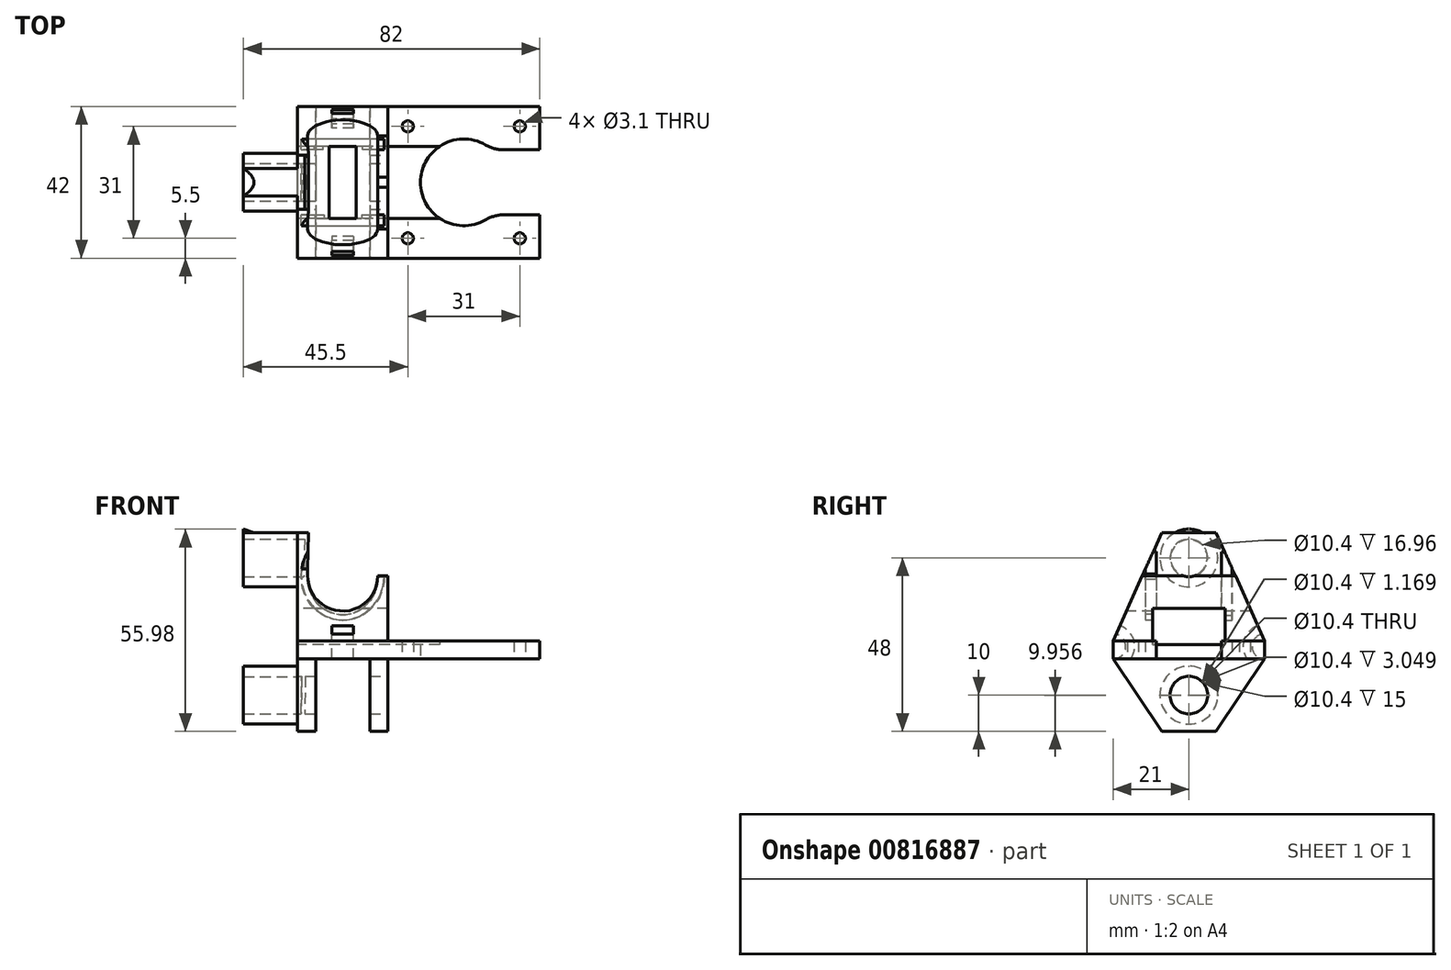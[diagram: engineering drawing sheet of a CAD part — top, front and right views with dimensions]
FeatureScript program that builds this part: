
annotation { "Feature Type Name" : "Feature", "Feature Type Description" : "" }
export const myFeature = defineFeature(function(context is Context, id is Id, definition is map)
    precondition{}
    {
        {
            var Q0;
            Q0=qCreatedBy(makeId("Top.planeOp"),FACE);
            var sketch = newSketch(context, id + "F0", { "sketchPlane" : qUnion([Q0])});
            skLineSegment(sketch, "E0.bottom", {"start": v(0, 0) * mm, "end": v(42, 0) * mm});
            skLineSegment(sketch, "E0.top", {"start": v(0, 42) * mm, "end": v(42, 42) * mm});
            skLineSegment(sketch, "E0.left", {"start": v(0, 0) * mm, "end": v(0, 42) * mm});
            skLineSegment(sketch, "E0.right", {"start": v(42, 0) * mm, "end": v(42, 12) * mm});
            skArc(sketch, "E1", {"start": v(27.05, 31.36) * mm, "mid": v(9, 21) * mm, "end": v(27.05, 10.64) * mm});
            skPoint(sketch, "E1.centerSnap0", {"position": v(21, 42) * mm});
            skPoint(sketch, "E1.centerSnap1", {"position": v(42, 21) * mm});
            skCircle(sketch, "E2", {"center": v(5.5, 36.5) * mm, "radius": 1.55 * mm});
            skCircle(sketch, "E3", {"center": v(36.5, 36.5) * mm, "radius": 1.55 * mm});
            skCircle(sketch, "E4", {"center": v(36.5, 5.5) * mm, "radius": 1.55 * mm});
            skCircle(sketch, "E5", {"center": v(5.5, 5.5) * mm, "radius": 1.55 * mm});
            skLineSegment(sketch, "E6", {"start": v(42, 30) * mm, "end": v(32.1, 30) * mm});
            skLineSegment(sketch, "E7", {"start": v(42, 12) * mm, "end": v(32.1, 12) * mm});
            skLineSegment(sketch, "E8.trimOffspring", {"start": v(42, 30) * mm, "end": v(42, 42) * mm});
            skPoint(sketch, "E9.visualSharp", {"position": v(28.94, 30) * mm});
            skArc(sketch, "E9.filletArc", {"start": v(27.05, 31.36) * mm, "mid": v(29.48, 30.35) * mm, "end": v(32.1, 30) * mm});
            skPoint(sketch, "E10.visualSharp", {"position": v(28.94, 12) * mm});
            skArc(sketch, "E10.filletArc", {"start": v(32.1, 12) * mm, "mid": v(29.48, 11.65) * mm, "end": v(27.05, 10.64) * mm});
            skSolve(sketch);
        }
        {
            var Q0;
            Q0 = qSketchRegion(id + "F0", true);
            extrude(context, id + "F1", {"entities" : qUnion([Q0]), "depth" : 5 * mm, "offsetDistance" : 25 * mm});
        }
        {
            var Q0;
            Q0=makeQuery(id+"F1.opExtrude","SWEPT_FACE",FACE,{"disambiguationData":[OSD([sQuery(id+"F0.wireOp",EDGE,"E0.left")])]});
            var sketch = newSketch(context, id + "F2", { "sketchPlane" : qUnion([Q0])});
            skLineSegment(sketch, "E11", {"start": v(-42, 5) * mm, "end": v(-28.5, 35) * mm});
            skLineSegment(sketch, "E12", {"start": v(-28.5, 35) * mm, "end": v(-13.5, 35) * mm});
            skLineSegment(sketch, "E13", {"start": v(-13.5, 35) * mm, "end": v(0, 5) * mm});
            skLineSegment(sketch, "E14", {"start": v(0, 5) * mm, "end": v(0, 0) * mm});
            skLineSegment(sketch, "E15", {"start": v(0, 0) * mm, "end": v(-13.5, -20) * mm});
            skLineSegment(sketch, "E16", {"start": v(-13.5, -20) * mm, "end": v(-28.5, -20) * mm});
            skLineSegment(sketch, "E17", {"start": v(-28.5, -20) * mm, "end": v(-42, 0) * mm});
            skLineSegment(sketch, "E18", {"start": v(-42, 0) * mm, "end": v(-42, 5) * mm});
            skLineSegment(sketch, "E19.bottom", {"start": v(-31, 5) * mm, "end": v(-11, 5) * mm});
            skLineSegment(sketch, "E19.top", {"start": v(-31, 13) * mm, "end": v(-11, 13) * mm});
            skLineSegment(sketch, "E19.left", {"start": v(-31, 5) * mm, "end": v(-31, 13) * mm});
            skLineSegment(sketch, "E19.right", {"start": v(-11, 5) * mm, "end": v(-11, 13) * mm});
            skCircle(sketch, "E20", {"center": v(-21, 28) * mm, "radius": 5.2 * mm});
            skPoint(sketch, "E20.centerSnap0", {"position": v(-21, 13) * mm});
            skCircle(sketch, "E21", {"center": v(-21, -10) * mm, "radius": 5.2 * mm});
            skPoint(sketch, "E21.centerSnap0", {"position": v(-21, 0) * mm});
            skSolve(sketch);
        }
        {
            var Q0;
            Q0 = qSketchRegion(id + "F2", true);
            extrude(context, id + "F3", {"entities" : qUnion([Q0]), "operationType" : NewBodyOperationType.ADD, "depth" : 25 * mm, "offsetDistance" : 25 * mm});
        }
        {
            var Q0;
            Q0=makeQuery(id+"F3.boolean.opBoolean","MERGE",FACE,{"derivedFrom":[makeQuery(id+"F1.opExtrude","SWEPT_FACE",FACE,{"disambiguationData":[OSD([sQuery(id+"F0.wireOp",EDGE,"E0.bottom")])]}),makeQuery(id+"F3.opExtrude","SWEPT_FACE",FACE,{"disambiguationData":[OSD([sQuery(id+"F2.wireOp",EDGE,"E14")])]})]});
            var sketch = newSketch(context, id + "F4", { "sketchPlane" : qUnion([Q0])});
            skArc(sketch, "E22", {"start": v(-22.25, 23.2) * mm, "mid": v(-12.6, 13.25) * mm, "end": v(-2.75, 23) * mm});
            skLineSegment(sketch, "E23.bottom", {"start": v(-20, 0) * mm, "end": v(-5, 0) * mm});
            skLineSegment(sketch, "E23.top", {"start": v(-20, -20) * mm, "end": v(-5, -20) * mm});
            skLineSegment(sketch, "E23.left", {"start": v(-20, 0) * mm, "end": v(-20, -20) * mm});
            skLineSegment(sketch, "E23.right", {"start": v(-5, 0) * mm, "end": v(-5, -20) * mm});
            skLineSegment(sketch, "E24", {"start": v(-2.75, 23) * mm, "end": v(0, 23) * mm});
            skLineSegment(sketch, "E25", {"start": v(0, 23) * mm, "end": v(0, 35.11) * mm});
            skLineSegment(sketch, "E26", {"start": v(0, 35.11) * mm, "end": v(-22, 35.11) * mm});
            skLineSegment(sketch, "E27", {"start": v(-22, 35.11) * mm, "end": v(-22.25, 23) * mm});
            skSolve(sketch);
        }
        {
            var Q0;
            Q0 = qSketchRegion(id + "F4", true);
            extrude(context, id + "F5", {"entities" : qUnion([Q0]), "operationType" : NewBodyOperationType.REMOVE, "oppositeDirection" : true, "depth" : 69 * mm, "offsetDistance" : 25 * mm});
        }
        {
            var Q0;
            Q0=makeQuery(id+"F3.opExtrude","CAP_FACE",FACE,{"disambiguationData":[OSD([sQuery(id+"F2.wireOp",EDGE,"E11"),sQuery(id+"F2.wireOp",EDGE,"E12"),sQuery(id+"F2.wireOp",EDGE,"E13"),sQuery(id+"F2.wireOp",EDGE,"E14"),sQuery(id+"F2.wireOp",EDGE,"E15"),sQuery(id+"F2.wireOp",EDGE,"E16"),sQuery(id+"F2.wireOp",EDGE,"E17"),sQuery(id+"F2.wireOp",EDGE,"E18"),sQuery(id+"F2.wireOp",EDGE,"E19.bottom"),sQuery(id+"F2.wireOp",EDGE,"E19.top"),sQuery(id+"F2.wireOp",EDGE,"E19.left"),sQuery(id+"F2.wireOp",EDGE,"E19.right"),sQuery(id+"F2.wireOp",EDGE,"E20"),sQuery(id+"F2.wireOp",EDGE,"E21")])],"isStart":false});
            var sketch = newSketch(context, id + "F6", { "sketchPlane" : qUnion([Q0])});
            skArc(sketch, "E28", {"start": v(-26.2, 28) * mm, "mid": v(-21, 22.8) * mm, "end": v(-15.8, 28) * mm});
            skArc(sketch, "E29", {"start": v(-29, 28) * mm, "mid": v(-21, 19.98) * mm, "end": v(-13, 28) * mm});
            skArc(sketch, "E30", {"start": v(-29, -10) * mm, "mid": v(-21, -18) * mm, "end": v(-13, -10) * mm});
            skArc(sketch, "E31", {"start": v(-26.2, -10) * mm, "mid": v(-21, -15.24) * mm, "end": v(-15.8, -10) * mm});
            skArc(sketch, "E32", {"start": v(-13, 28) * mm, "mid": v(-21, 35.98) * mm, "end": v(-29, 28) * mm});
            skArc(sketch, "E33", {"start": v(-15.8, 28) * mm, "mid": v(-21, 33.2) * mm, "end": v(-26.2, 28) * mm});
            skArc(sketch, "E34", {"start": v(-13, -10) * mm, "mid": v(-21, -2) * mm, "end": v(-29, -10) * mm});
            skArc(sketch, "E35", {"start": v(-15.8, -10) * mm, "mid": v(-21, -4.84) * mm, "end": v(-26.2, -10) * mm});
            skSolve(sketch);
        }
        {
            var Q0;
            Q0 = qSketchRegion(id + "F6", true);
            extrude(context, id + "F7", {"entities" : qUnion([Q0]), "operationType" : NewBodyOperationType.ADD, "depth" : 15 * mm, "offsetDistance" : 25 * mm});
        }
        {
            var Q0;
            Q0=makeQuery(id+"F3.boolean.opBoolean","MERGE",FACE,{"derivedFrom":[makeQuery(id+"F1.opExtrude","SWEPT_FACE",FACE,{"disambiguationData":[OSD([sQuery(id+"F0.wireOp",EDGE,"E0.bottom")])]}),makeQuery(id+"F3.opExtrude","SWEPT_FACE",FACE,{"disambiguationData":[OSD([sQuery(id+"F2.wireOp",EDGE,"E14")])]})]});
            cPlane(context, id + "F8", {"entities" : qUnion([Q0]), "cplaneType" : CPlaneType.OFFSET, "offset" : 9 * mm, "oppositeDirection" : true, "width" : 150 * mm, "height" : 150 * mm});
        }
        {
            var Q0;
            Q0=qCreatedBy(id+"F8.planeOp",FACE);
            var sketch = newSketch(context, id + "F9", { "sketchPlane" : qUnion([Q0])});
            skEllipse(sketch, "E36", {"center": v(-12.5, 23.1) * mm, "majorRadius": 10.75 * mm, "minorRadius": 9.75 * mm, "majorAxis": v(0, -1)});
            skEllipse(sketch, "E37", {"center": v(-12.5, 23.1) * mm, "majorRadius": 12.25 * mm, "minorRadius": 11.5 * mm, "majorAxis": v(0, -1)});
            skSolve(sketch);
        }
        {
            var Q0;
            Q0 = qSketchRegion(id + "F9", true);
            extrude(context, id + "F10", {"entities" : qUnion([Q0]), "operationType" : NewBodyOperationType.REMOVE, "oppositeDirection" : true, "depth" : 3 * mm, "offsetDistance" : 25 * mm});
        }
        {
            var Q0;
            Q0=makeQuery(id+"F3.boolean.opBoolean","MERGE",FACE,{"derivedFrom":[makeQuery(id+"F1.opExtrude","SWEPT_FACE",FACE,{"disambiguationData":[OSD([sQuery(id+"F0.wireOp",EDGE,"E0.top")])]}),makeQuery(id+"F3.opExtrude","SWEPT_FACE",FACE,{"disambiguationData":[OSD([sQuery(id+"F2.wireOp",EDGE,"E18")])]})]});
            cPlane(context, id + "F11", {"entities" : qUnion([Q0]), "cplaneType" : CPlaneType.OFFSET, "offset" : 9 * mm, "oppositeDirection" : true, "width" : 150 * mm, "height" : 150 * mm});
        }
        {
            var Q0;
            Q0=qCreatedBy(id+"F11.planeOp",FACE);
            var sketch = newSketch(context, id + "F12", { "sketchPlane" : qUnion([Q0])});
            skEllipse(sketch, "E38", {"center": v(12.5, 22.9) * mm, "majorRadius": 10.75 * mm, "minorRadius": 9.75 * mm, "majorAxis": v(0, -1)});
            skEllipse(sketch, "E39", {"center": v(12.5, 22.9) * mm, "majorRadius": 12.25 * mm, "minorRadius": 11.5 * mm, "majorAxis": v(0, -1)});
            skSolve(sketch);
        }
        {
            var Q0;
            Q0 = qSketchRegion(id + "F12", true);
            extrude(context, id + "F13", {"entities" : qUnion([Q0]), "operationType" : NewBodyOperationType.REMOVE, "oppositeDirection" : true, "depth" : 3 * mm, "offsetDistance" : 25 * mm});
        }
        {
            var Q0;
            {var subQ0=sQuery(id+"F0.wireOp",EDGE,"E0.bottom");var subQ1=sQuery(id+"F2.wireOp",EDGE,"E21");var subQ2=sQuery(id+"F2.wireOp",EDGE,"E20");var subQ3=sQuery(id+"F2.wireOp",EDGE,"E19.top");var subQ4=sQuery(id+"F2.wireOp",EDGE,"E18");var subQ5=sQuery(id+"F2.wireOp",EDGE,"E17");var subQ6=sQuery(id+"F2.wireOp",EDGE,"E11");var subQ7=sQuery(id+"F6.wireOp",EDGE,"j4Je13ar-cUgQ-P9dA-qSxm-OQoqqm40TVXU");var subQ8=sQuery(id+"F2.wireOp",EDGE,"E19.right");var subQ9=sQuery(id+"F0.wireOp",EDGE,"E0.top");var subQ10=sQuery(id+"F6.wireOp",EDGE,"E31");var subQ11=sQuery(id+"F6.wireOp",EDGE,"E30");var subQ12=sQuery(id+"F6.wireOp",EDGE,"HeXZzPOW-6o9y-4eNm-dmXj-kad8RJGDjiKm");var subQ13=sQuery(id+"F2.wireOp",EDGE,"E19.left");var subQ14=sQuery(id+"F2.wireOp",EDGE,"E19.bottom");var subQ15=sQuery(id+"F2.wireOp",EDGE,"E15");var subQ16=sQuery(id+"F2.wireOp",EDGE,"E16");var subQ17=sQuery(id+"F2.wireOp",EDGE,"E14");var subQ18=sQuery(id+"F2.wireOp",EDGE,"E13");var subQ19=sQuery(id+"F2.wireOp",EDGE,"E12");var subQ20=makeQuery(id+"F3.opExtrude","CAP_FACE",FACE,{"disambiguationData":[OSD([subQ6,subQ19,subQ18,subQ17,subQ15,subQ16,subQ5,subQ4,subQ14,subQ3,subQ13,subQ8,subQ2,subQ1])],"isStart":false});Q0=makeQuery(id+"F7.boolean.opBoolean","SPLIT",FACE,{"disambiguationData":[TD([makeQuery(id+"F1.opExtrude","SWEPT_FACE",FACE,{"disambiguationData":[OSD([subQ0])]}),makeQuery(id+"F1.opExtrude","CAP_FACE",FACE,{"disambiguationData":[OSD([subQ0,subQ9,sQuery(id+"F0.wireOp",EDGE,"E0.left"),sQuery(id+"F0.wireOp",EDGE,"E0.right"),sQuery(id+"F0.wireOp",EDGE,"E1"),sQuery(id+"F0.wireOp",EDGE,"E2"),sQuery(id+"F0.wireOp",EDGE,"E3"),sQuery(id+"F0.wireOp",EDGE,"E4"),sQuery(id+"F0.wireOp",EDGE,"E5"),sQuery(id+"F0.wireOp",EDGE,"E6"),sQuery(id+"F0.wireOp",EDGE,"E7"),sQuery(id+"F0.wireOp",EDGE,"E8.trimOffspring"),sQuery(id+"F0.wireOp",EDGE,"E9.filletArc"),sQuery(id+"F0.wireOp",EDGE,"E10.filletArc")])],"isStart":false}),makeQuery(id+"F1.opExtrude","SWEPT_FACE",FACE,{"disambiguationData":[OSD([subQ9])]}),makeQuery(id+"F3.opExtrude","SWEPT_FACE",FACE,{"disambiguationData":[OSD([subQ6])]}),subQ20,makeQuery(id+"F3.opExtrude","SWEPT_FACE",FACE,{"disambiguationData":[OSD([subQ19])]}),makeQuery(id+"F3.opExtrude","SWEPT_FACE",FACE,{"disambiguationData":[OSD([subQ18])]}),makeQuery(id+"F3.opExtrude","SWEPT_FACE",FACE,{"disambiguationData":[OSD([subQ17])]}),makeQuery(id+"F3.opExtrude","SWEPT_FACE",FACE,{"disambiguationData":[OSD([subQ15])]}),makeQuery(id+"F3.opExtrude","SWEPT_FACE",FACE,{"disambiguationData":[OSD([subQ16])]}),makeQuery(id+"F3.opExtrude","SWEPT_FACE",FACE,{"disambiguationData":[OSD([subQ5])]}),makeQuery(id+"F3.opExtrude","SWEPT_FACE",FACE,{"disambiguationData":[OSD([subQ4])]}),makeQuery(id+"F3.opExtrude","SWEPT_FACE",FACE,{"disambiguationData":[OSD([subQ14])]}),makeQuery(id+"F3.opExtrude","SWEPT_FACE",FACE,{"disambiguationData":[OSD([subQ3])]}),makeQuery(id+"F3.opExtrude","SWEPT_FACE",FACE,{"disambiguationData":[OSD([subQ13])]}),makeQuery(id+"F3.opExtrude","SWEPT_FACE",FACE,{"disambiguationData":[OSD([subQ8])]}),makeQuery(id+"F3.opExtrude","SWEPT_FACE",FACE,{"disambiguationData":[OSD([subQ2])]}),makeQuery(id+"F3.opExtrude","SWEPT_FACE",FACE,{"disambiguationData":[OSD([subQ1])]}),makeQuery(id+"F7.opExtrude","SWEPT_FACE",FACE,{"disambiguationData":[OSD([sQuery(id+"F6.wireOp",EDGE,"1yMtYrWf-nUJP-NBpX-7LZj-JU54sDcnYQW7")])]}),makeQuery(id+"F7.opExtrude","SWEPT_FACE",FACE,{"disambiguationData":[OSD([sQuery(id+"F6.wireOp",EDGE,"Y7kda9e2-xFBF-SAdd-E8dt-nTogyCoIO5LO")])]}),makeQuery(id+"F7.opExtrude","SWEPT_FACE",FACE,{"disambiguationData":[OSD([sQuery(id+"F6.wireOp",EDGE,"E28")])]}),makeQuery(id+"F7.opExtrude","SWEPT_FACE",FACE,{"disambiguationData":[OSD([sQuery(id+"F6.wireOp",EDGE,"E29")])]}),makeQuery(id+"F7.opExtrude","SWEPT_FACE",FACE,{"disambiguationData":[OSD([subQ12])]}),makeQuery(id+"F7.opExtrude","CAP_FACE",FACE,{"disambiguationData":[OSD([subQ12,subQ11,subQ7,subQ10])],"isStart":true}),makeQuery(id+"F7.opExtrude","SWEPT_FACE",FACE,{"disambiguationData":[OSD([subQ11])]}),makeQuery(id+"F7.opExtrude","SWEPT_FACE",FACE,{"disambiguationData":[OSD([subQ7])]}),makeQuery(id+"F7.opExtrude","SWEPT_FACE",FACE,{"disambiguationData":[OSD([subQ10])]})])],"derivedFrom":subQ20});}
            cPlane(context, id + "F14", {"entities" : qUnion([Q0]), "cplaneType" : CPlaneType.OFFSET, "offset" : 9.5 * mm, "oppositeDirection" : true, "width" : 150 * mm, "height" : 150 * mm});
        }
        {
            var Q0;
            Q0=qCreatedBy(id+"F14.planeOp",FACE);
            var sketch = newSketch(context, id + "F15", { "sketchPlane" : qUnion([Q0])});
            skCircle(sketch, "E40", {"center": v(0, 3.5) * mm, "radius": 3.5 * mm});
            skCircle(sketch, "E41", {"center": v(0, 3.5) * mm, "radius": 6 * mm});
            skCircle(sketch, "E42", {"center": v(-42, 3.5) * mm, "radius": 3.5 * mm});
            skCircle(sketch, "E43", {"center": v(-42, 3.5) * mm, "radius": 6 * mm});
            skSolve(sketch);
        }
        {
            var Q0;
            Q0 = qSketchRegion(id + "F15", true);
            extrude(context, id + "F16", {"entities" : qUnion([Q0]), "operationType" : NewBodyOperationType.REMOVE, "oppositeDirection" : true, "depth" : 6 * mm, "offsetDistance" : 25 * mm});
        }
        {
            var Q0;
            {var subQ0=sQuery(id+"F2.wireOp",EDGE,"E16");var subQ1=sQuery(id+"F2.wireOp",EDGE,"E14");var subQ2=sQuery(id+"F2.wireOp",EDGE,"E13");var subQ3=sQuery(id+"F2.wireOp",EDGE,"E12");var subQ4=sQuery(id+"F2.wireOp",EDGE,"E15");var subQ5=sQuery(id+"F0.wireOp",EDGE,"E0.bottom");var subQ6=sQuery(id+"F2.wireOp",EDGE,"E19.bottom");var subQ7=sQuery(id+"F2.wireOp",EDGE,"E17");var subQ9=sQuery(id+"F2.wireOp",EDGE,"E19.left");var subQ12=sQuery(id+"F2.wireOp",EDGE,"E19.right");var subQ13=sQuery(id+"F2.wireOp",EDGE,"E11");var subQ14=sQuery(id+"F2.wireOp",EDGE,"E18");var subQ15=sQuery(id+"F2.wireOp",EDGE,"E19.top");Q0=makeQuery(id+"F7.boolean.opBoolean","SPLIT",FACE,{"disambiguationData":[TD([makeQuery(id+"F1.opExtrude","SWEPT_FACE",FACE,{"disambiguationData":[OSD([subQ5])]})])],"derivedFrom":makeQuery(id+"F3.opExtrude","CAP_FACE",FACE,{"disambiguationData":[OSD([subQ13,subQ3,subQ2,subQ1,subQ4,subQ0,subQ7,subQ14,subQ6,subQ15,subQ9,subQ12,sQuery(id+"F2.wireOp",EDGE,"E20"),sQuery(id+"F2.wireOp",EDGE,"E21")])],"isStart":false})});}
            var sketch = newSketch(context, id + "F17", { "sketchPlane" : qUnion([Q0])});
            skLineSegment(sketch, "E44.bottom", {"start": v(-31, 4) * mm, "end": v(-11, 4) * mm});
            skLineSegment(sketch, "E44.top", {"start": v(-31, 14) * mm, "end": v(-11, 14) * mm});
            skLineSegment(sketch, "E44.left", {"start": v(-31, 4) * mm, "end": v(-31, 14) * mm});
            skLineSegment(sketch, "E44.right", {"start": v(-11, 4) * mm, "end": v(-11, 14) * mm});
            skSolve(sketch);
        }
        {
            var Q0;
            Q0 = qSketchRegion(id + "F17", true);
            extrude(context, id + "F18", {"entities" : qUnion([Q0]), "operationType" : NewBodyOperationType.REMOVE, "oppositeDirection" : true, "depth" : 50 * mm, "offsetDistance" : 25 * mm});
        }
        {
            var Q0;
            {var subQ0=sQuery(id+"F6.wireOp",EDGE,"E32");var subQ1=sQuery(id+"F6.wireOp",EDGE,"E29");Q0=makeQuery(id+"F7.boolean.opBoolean","SPLIT",EDGE,{"disambiguationData":[topologyDisambiguationEdgeConnected([makeQuery(id+"F3.opExtrude","CAP_FACE",FACE,{"disambiguationData":[OSD([sQuery(id+"F2.wireOp",EDGE,"E11"),sQuery(id+"F2.wireOp",EDGE,"E12"),sQuery(id+"F2.wireOp",EDGE,"E13"),sQuery(id+"F2.wireOp",EDGE,"E14"),sQuery(id+"F2.wireOp",EDGE,"E15"),sQuery(id+"F2.wireOp",EDGE,"E16"),sQuery(id+"F2.wireOp",EDGE,"E17"),sQuery(id+"F2.wireOp",EDGE,"E18"),sQuery(id+"F2.wireOp",EDGE,"E19.bottom"),sQuery(id+"F2.wireOp",EDGE,"E19.top"),sQuery(id+"F2.wireOp",EDGE,"E19.left"),sQuery(id+"F2.wireOp",EDGE,"E19.right"),sQuery(id+"F2.wireOp",EDGE,"E20"),sQuery(id+"F2.wireOp",EDGE,"E21")])],"isStart":false})])],"derivedFrom":makeQuery(id+"F7.opExtrude","CAP_EDGE",EDGE,{"disambiguationData":[OSD([subQ1,subQ0])],"isStart":true})});}
            var Q1;
            Q1=makeQuery(id+"F7.opExtrude","CAP_EDGE",EDGE,{"disambiguationData":[OSD([sQuery(id+"F6.wireOp",EDGE,"E30"),sQuery(id+"F6.wireOp",EDGE,"E34")])],"isStart":true});
            chamfer(context, id + "F19", {"entities" : qUnion([Q0, Q1]), "chamferType" : ChamferType.TWO_OFFSETS, "width1" : 15 * mm, "oppositeDirection" : false, "width2" : 5 * mm, "tangentPropagation" : true});
        }
        {
            var Q0;
            {var subQ4=makeQuery(id+"F5.boolean.opBoolean","COPY",FACE,{"derivedFrom":makeQuery(id+"F5.opExtrude","SWEPT_FACE",FACE,{"disambiguationData":[OSD([sQuery(id+"F4.wireOp",EDGE,"E27")])]})});Q0=makeQuery(id+"F13.boolean.opBoolean","SPLIT",FACE,{"disambiguationData":[TD([makeQuery(id+"F3.opExtrude","SWEPT_FACE",FACE,{"disambiguationData":[OSD([sQuery(id+"F2.wireOp",EDGE,"E12")])]})])],"derivedFrom":subQ4});}
            var sketch = newSketch(context, id + "F20", { "sketchPlane" : qUnion([Q0])});
            skLineSegment(sketch, "E45.bottom", {"start": v(13.6, 0) * mm, "end": v(29.55, 0) * mm});
            skLineSegment(sketch, "E45.top", {"start": v(13.6, -17.05) * mm, "end": v(29.55, -17.05) * mm});
            skLineSegment(sketch, "E45.left", {"start": v(13.6, 0) * mm, "end": v(13.6, -17.05) * mm});
            skLineSegment(sketch, "E45.right", {"start": v(29.55, 0) * mm, "end": v(29.55, -17.05) * mm});
            skLineSegment(sketch, "E46.bottom", {"start": v(13.5, 34.53) * mm, "end": v(28.12, 34.53) * mm});
            skLineSegment(sketch, "E46.top", {"start": v(13.5, 19.84) * mm, "end": v(28.12, 19.84) * mm});
            skLineSegment(sketch, "E46.left", {"start": v(13.5, 34.53) * mm, "end": v(13.5, 19.84) * mm});
            skLineSegment(sketch, "E46.right", {"start": v(28.12, 34.53) * mm, "end": v(28.12, 19.84) * mm});
            skSolve(sketch);
        }
        {
            var Q0;
            Q0 = qSketchRegion(id + "F20", true);
            extrude(context, id + "F21", {"entities" : qUnion([Q0]), "operationType" : NewBodyOperationType.ADD, "oppositeDirection" : true, "depth" : 1 * mm, "offsetDistance" : 25 * mm});
        }
    });
